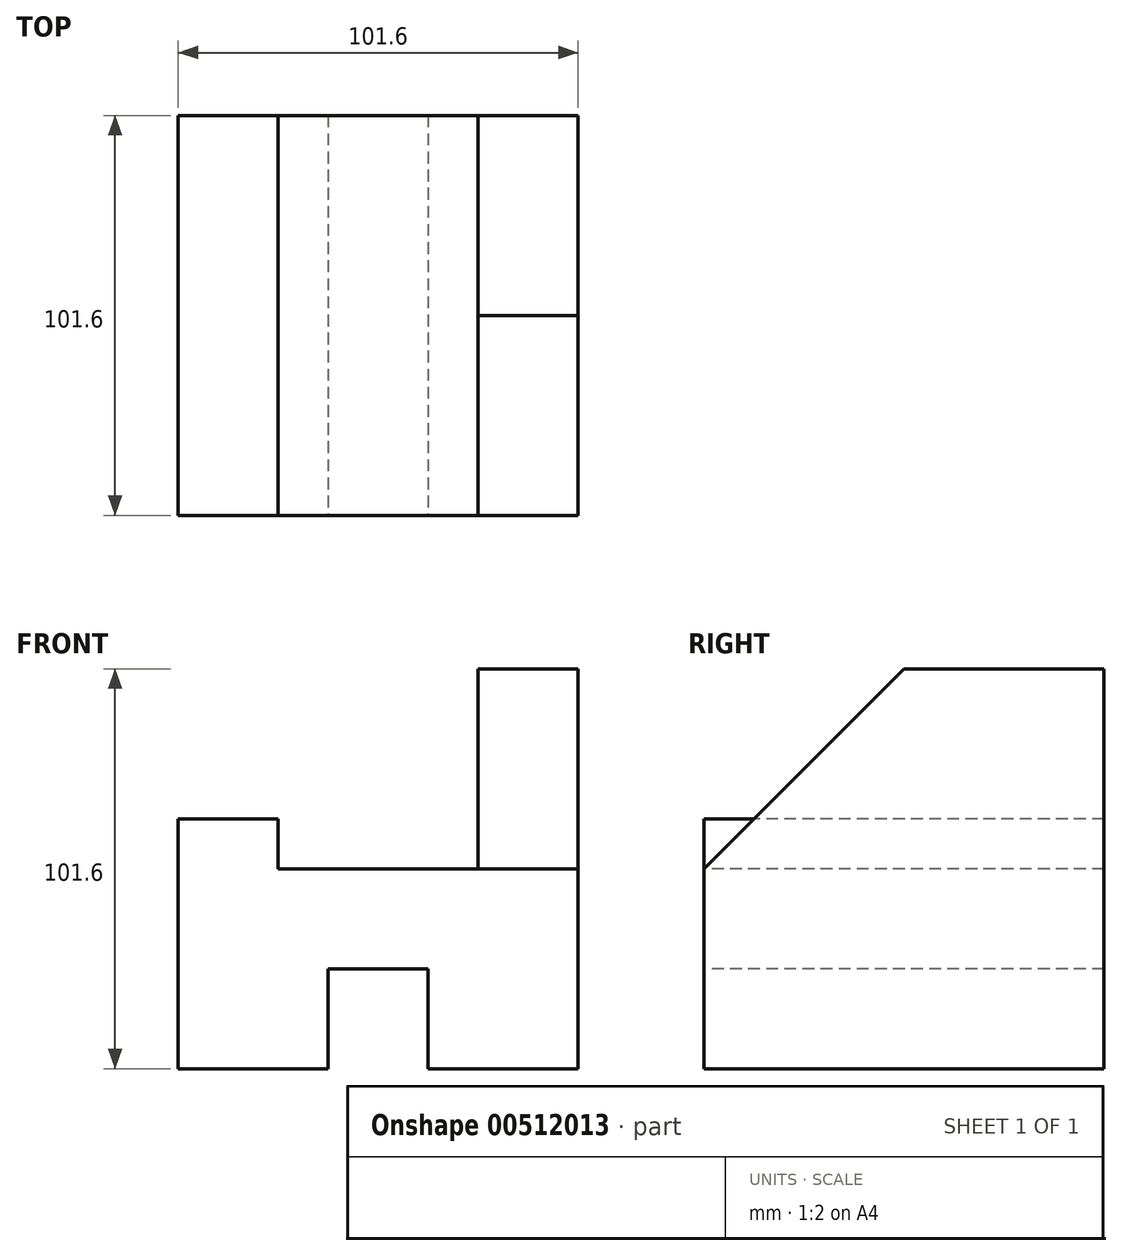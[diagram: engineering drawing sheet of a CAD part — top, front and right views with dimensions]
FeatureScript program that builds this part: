
annotation { "Feature Type Name" : "Feature", "Feature Type Description" : "" }
export const myFeature = defineFeature(function(context is Context, id is Id, definition is map)
    precondition{}
    {
        {
            var Q0;
            Q0=qCreatedBy(makeId("Front.planeOp"),FACE);
            var sketch = newSketch(context, id + "F0", { "sketchPlane" : qUnion([Q0])});
            skLineSegment(sketch, "E0.bottom", {"start": v(0, 0) * mm, "end": v(-101.6, 0) * mm});
            skLineSegment(sketch, "E0.top", {"start": v(0, 101.6) * mm, "end": v(-101.6, 101.6) * mm});
            skLineSegment(sketch, "E0.left", {"start": v(0, 0) * mm, "end": v(0, 101.6) * mm});
            skLineSegment(sketch, "E0.right", {"start": v(-101.6, 0) * mm, "end": v(-101.6, 101.6) * mm});
            skSolve(sketch);
        }
        {
            var Q0;
            Q0=makeQuery(id+"F0.imprint","IMPRINT",FACE,{"disambiguationData":[TD([[makeQuery(id+"F0.imprint","IMPRINT",EDGE,{"derivedFrom":sQuery(id+"F0.wireOp",EDGE,"E0.bottom")}),-1.0]])]});
            extrude(context, id + "F1", {"entities" : qUnion([Q0]), "depth" : 101.6 * mm});
        }
        {
            var Q0;
            Q0=makeQuery(id+"F1.opExtrude","CAP_FACE",FACE,{"disambiguationData":[OSD([sQuery(id+"F0.wireOp",EDGE,"E0.bottom"),sQuery(id+"F0.wireOp",EDGE,"E0.top"),sQuery(id+"F0.wireOp",EDGE,"E0.left"),sQuery(id+"F0.wireOp",EDGE,"E0.right")])],"isStart":false});
            var sketch = newSketch(context, id + "F2", { "sketchPlane" : qUnion([Q0])});
            skLineSegment(sketch, "E1", {"start": v(-101.6, 0) * mm, "end": v(-63.5, 0) * mm});
            skLineSegment(sketch, "E2", {"start": v(-63.5, 0) * mm, "end": v(-63.5, 25.4) * mm});
            skLineSegment(sketch, "E3", {"start": v(-63.5, 25.4) * mm, "end": v(-38.1, 25.4) * mm});
            skLineSegment(sketch, "E4", {"start": v(-38.1, 25.4) * mm, "end": v(-38.1, 0) * mm});
            skLineSegment(sketch, "E5", {"start": v(-38.1, 0) * mm, "end": v(0, 0) * mm});
            skSolve(sketch);
        }
        {
            var Q0;
            {var subQ0=sQuery(id+"F2.wireOp",EDGE,"E2");Q0=makeQuery(id+"F2.imprint","IMPRINT",FACE,{"disambiguationData":[TD([[makeQuery(id+"F2.imprint","IMPRINT",EDGE,{"derivedFrom":subQ0}),-1.0]])]});}
            extrude(context, id + "F3", {"entities" : qUnion([Q0]), "operationType" : NewBodyOperationType.REMOVE, "oppositeDirection" : true, "depth" : 1955.8 * mm});
        }
        {
            var Q0;
            Q0=makeQuery(id+"F1.opExtrude","CAP_FACE",FACE,{"disambiguationData":[OSD([sQuery(id+"F0.wireOp",EDGE,"E0.bottom"),sQuery(id+"F0.wireOp",EDGE,"E0.top"),sQuery(id+"F0.wireOp",EDGE,"E0.left"),sQuery(id+"F0.wireOp",EDGE,"E0.right")])],"isStart":false});
            var sketch = newSketch(context, id + "F4", { "sketchPlane" : qUnion([Q0])});
            skLineSegment(sketch, "E6", {"start": v(-101.6, 101.6) * mm, "end": v(-101.6, 63.5) * mm});
            skLineSegment(sketch, "E7", {"start": v(-101.6, 63.5) * mm, "end": v(-76.2, 63.5) * mm});
            skLineSegment(sketch, "E8", {"start": v(-76.2, 63.5) * mm, "end": v(-76.2, 101.6) * mm});
            skSolve(sketch);
        }
        {
            var Q0;
            {var subQ0=sQuery(id+"F4.wireOp",EDGE,"E6");Q0=makeQuery(id+"F4.imprint","IMPRINT",FACE,{"disambiguationData":[TD([[makeQuery(id+"F4.imprint","IMPRINT",EDGE,{"derivedFrom":subQ0}),-1.0]])]});}
            extrude(context, id + "F5", {"entities" : qUnion([Q0]), "operationType" : NewBodyOperationType.REMOVE, "oppositeDirection" : true, "depth" : 101.6 * mm});
        }
        {
            var Q0;
            Q0=makeQuery(id+"F1.opExtrude","CAP_FACE",FACE,{"disambiguationData":[OSD([sQuery(id+"F0.wireOp",EDGE,"E0.bottom"),sQuery(id+"F0.wireOp",EDGE,"E0.top"),sQuery(id+"F0.wireOp",EDGE,"E0.left"),sQuery(id+"F0.wireOp",EDGE,"E0.right")])],"isStart":false});
            var sketch = newSketch(context, id + "F6", { "sketchPlane" : qUnion([Q0])});
            skLineSegment(sketch, "E9", {"start": v(-76.2, 63.5) * mm, "end": v(-76.2, 50.8) * mm});
            skLineSegment(sketch, "E10", {"start": v(-76.2, 50.8) * mm, "end": v(-25.4, 50.8) * mm});
            skLineSegment(sketch, "E11", {"start": v(-25.4, 50.8) * mm, "end": v(-25.4, 101.6) * mm});
            skSolve(sketch);
        }
        {
            var Q0;
            Q0=makeQuery(id+"F6.imprint","IMPRINT",FACE,{"disambiguationData":[TD([[makeQuery(id+"F6.imprint","IMPRINT",EDGE,{"derivedFrom":sQuery(id+"F6.wireOp",EDGE,"E9")}),1.0]])]});
            extrude(context, id + "F7", {"entities" : qUnion([Q0]), "operationType" : NewBodyOperationType.REMOVE, "oppositeDirection" : true, "depth" : 1955.8 * mm});
        }
        {
            var Q0;
            Q0=makeQuery(id+"F1.opExtrude","SWEPT_FACE",FACE,{"disambiguationData":[OSD([sQuery(id+"F0.wireOp",EDGE,"E0.left")])]});
            var sketch = newSketch(context, id + "F8", { "sketchPlane" : qUnion([Q0])});
            skLineSegment(sketch, "E12", {"start": v(-101.6, 0) * mm, "end": v(-101.6, 50.8) * mm});
            skLineSegment(sketch, "E13", {"start": v(-101.6, 50.8) * mm, "end": v(-50.8, 101.6) * mm});
            skSolve(sketch);
        }
        {
            var Q0;
            {var subQ0=sQuery(id+"F8.wireOp",EDGE,"E13");Q0=makeQuery(id+"F8.imprint","IMPRINT",FACE,{"disambiguationData":[TD([[makeQuery(id+"F8.imprint","IMPRINT",EDGE,{"derivedFrom":subQ0}),1.0]])]});}
            extrude(context, id + "F9", {"entities" : qUnion([Q0]), "operationType" : NewBodyOperationType.REMOVE, "oppositeDirection" : true, "depth" : 25.4 * mm});
        }
    });
